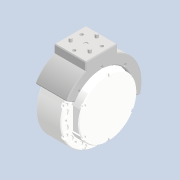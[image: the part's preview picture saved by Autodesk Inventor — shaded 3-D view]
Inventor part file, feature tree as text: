
AUTODESK INVENTOR PART (.ipt)
format: ipt  version: 2020.2 (Build 242310000, 310)  size: 2,347,008 bytes
history: native  units: in
note: dims shown in document units (in); Inventor stores cm internally (conversion verified against a paired STEP export)
features: other x15, move_body x3, extrude x1, sketch x1
ambient origin geometry x8: Origin, YZ Plane, XZ Plane, XY Plane, X Axis, Y Axis, Z Axis, Center Point
bodies: Solid1 (feature_tree)
feature tree (20):
  other  "Ensamble Final.iam"
  other  "Acople Aductor.ipt:1"
  other  "DIN 963 - M4 x 14.ipt:1"
  other  "DIN 963 - M4 x 14.ipt:2"
  other  "DIN 963 - M4 x 14.ipt:3"
  other  "DIN 916 - M4  x  8.ipt:1"
  other  "DIN 916 - M4  x  8.ipt:2"
  other  "DIN 916 - M4  x  8.ipt:3"
  other  "DIN 916 - M4  x  8.ipt:4"
  other  "DIN 916 - M4  x  8.ipt:5"
  other  "DIN 916 - M4  x  8.ipt:6"
  other  "DIN 916 - M4  x  8.ipt:7"
  other  "DIN 916 - M4  x  8.ipt:8"
  other  "Ensamble Pierna.Arnés13.iam:1::Ensamble Pierna.Arnés13.ipt:1"
  other  "Motor.ipt:2"
  extrude  "Extrusion1"  Depth=0.1969in
  move_body  "Move Body1"
  move_body  "Move Body2"
  move_body  "Move Body3"
  sketch  "Sketch1"  dims[d0=0.3937in d1=0.1969in d2=0.0394in d3=0.0in d4=2.8022in d5=-8.5765in d6=0.0in d7=90.0deg d8=0.0in d9=0.0in d10=9.3639in]
